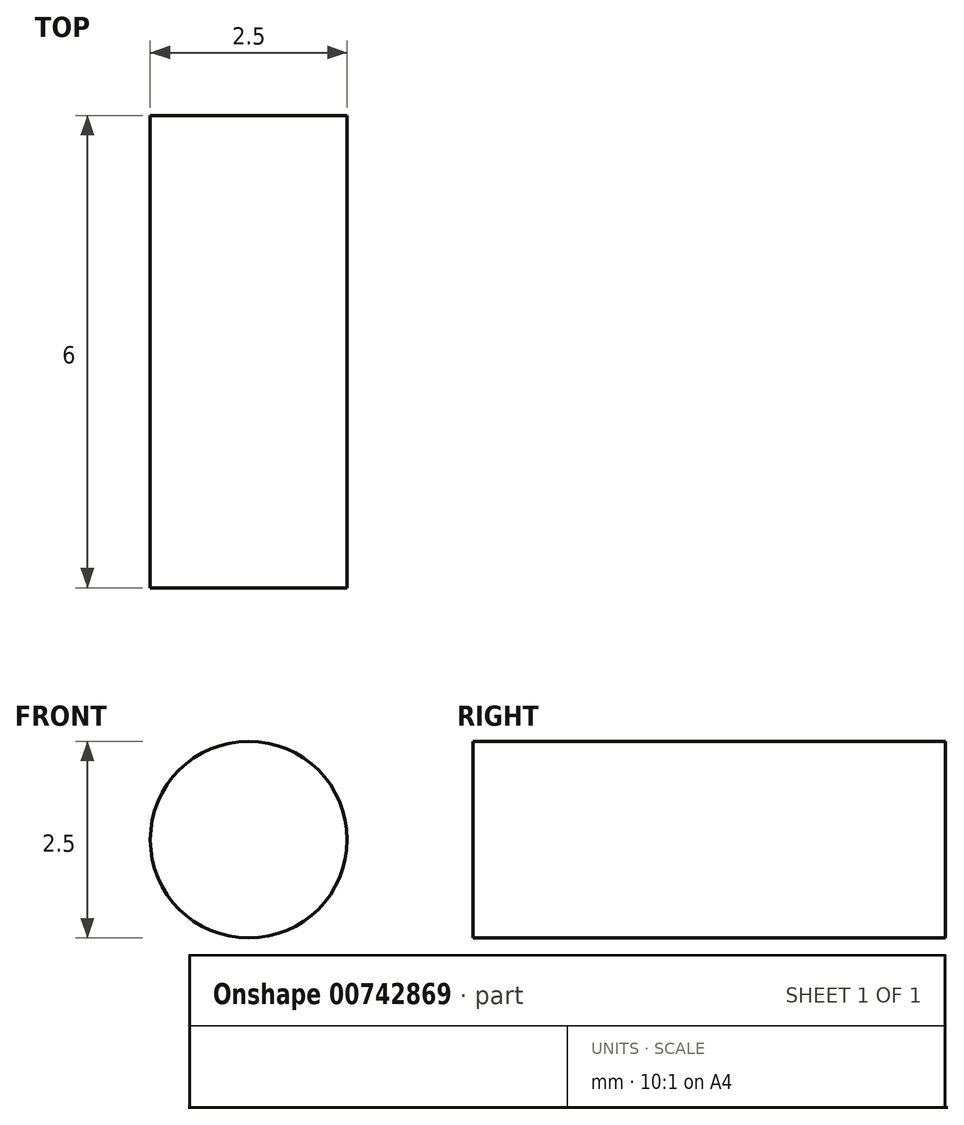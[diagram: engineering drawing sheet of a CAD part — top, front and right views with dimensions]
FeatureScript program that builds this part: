
annotation { "Feature Type Name" : "Feature", "Feature Type Description" : "" }
export const myFeature = defineFeature(function(context is Context, id is Id, definition is map)
    precondition{}
    {
        {
            var Q0;
            Q0=qCreatedBy(makeId("Front.planeOp"),FACE);
            var sketch = newSketch(context, id + "F0", { "sketchPlane" : qUnion([Q0])});
            skCircle(sketch, "E0", {"center": v(0, 0) * mm, "radius": 1.25 * mm});
            skSolve(sketch);
        }
        {
            var Q0;
            Q0 = qSketchRegion(id + "F0", true);
            extrude(context, id + "F1", {"entities" : qUnion([Q0]), "depth" : 6 * mm, "offsetDistance" : 25 * mm});
        }
    });
